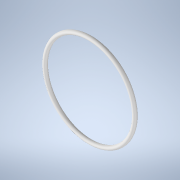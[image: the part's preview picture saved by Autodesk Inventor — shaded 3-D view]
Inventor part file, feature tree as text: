
AUTODESK INVENTOR PART (.ipt)
format: ipt  version: 2022 (Build 260153000, 153)  size: 121,856 bytes
history: native  units: mm
features: revolve x1, sketch x1
ambient origin geometry x8: Origin, YZ Plane, XZ Plane, XY Plane, X Axis, Y Axis, Z Axis, Center Point
bodies: Volumenkörper1 (feature_tree)
feature tree (2):
  revolve  "Umdrehung1"
  sketch  "Skizze1"  dims[d2=90.0deg d5=27.75mm]
